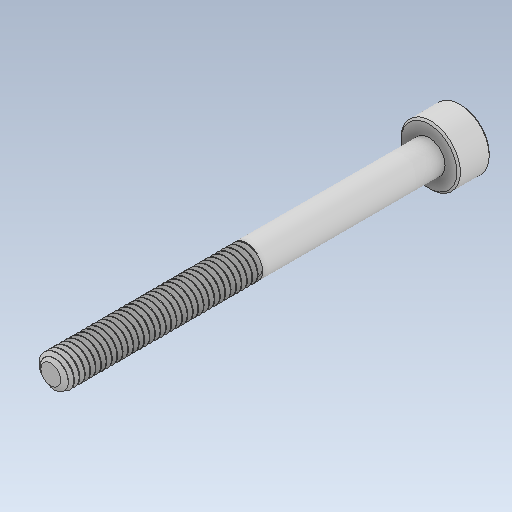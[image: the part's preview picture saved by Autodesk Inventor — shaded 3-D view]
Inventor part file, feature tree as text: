
AUTODESK INVENTOR PART (.ipt)
format: ipt  version: 2020 (Build 240168000, 168)  size: 1,009,664 bytes
history: native  units: in
note: dims shown in document units (in); Inventor stores cm internally (conversion verified against a paired STEP export)
features: revolve x1
ambient origin geometry x8: Origin, YZ Plane, XZ Plane, XY Plane, X Axis, Y Axis, Z Axis, Center Point
bodies: Solid1 (feature_tree)
feature tree (1):
  revolve  "Revolve1"  [1 undecoded]
note: 1 required parameter value undecoded (feature->parameter linkage not recoverable at this tier; creation-order binding heuristic only, values carry confidence <= 0.55)
